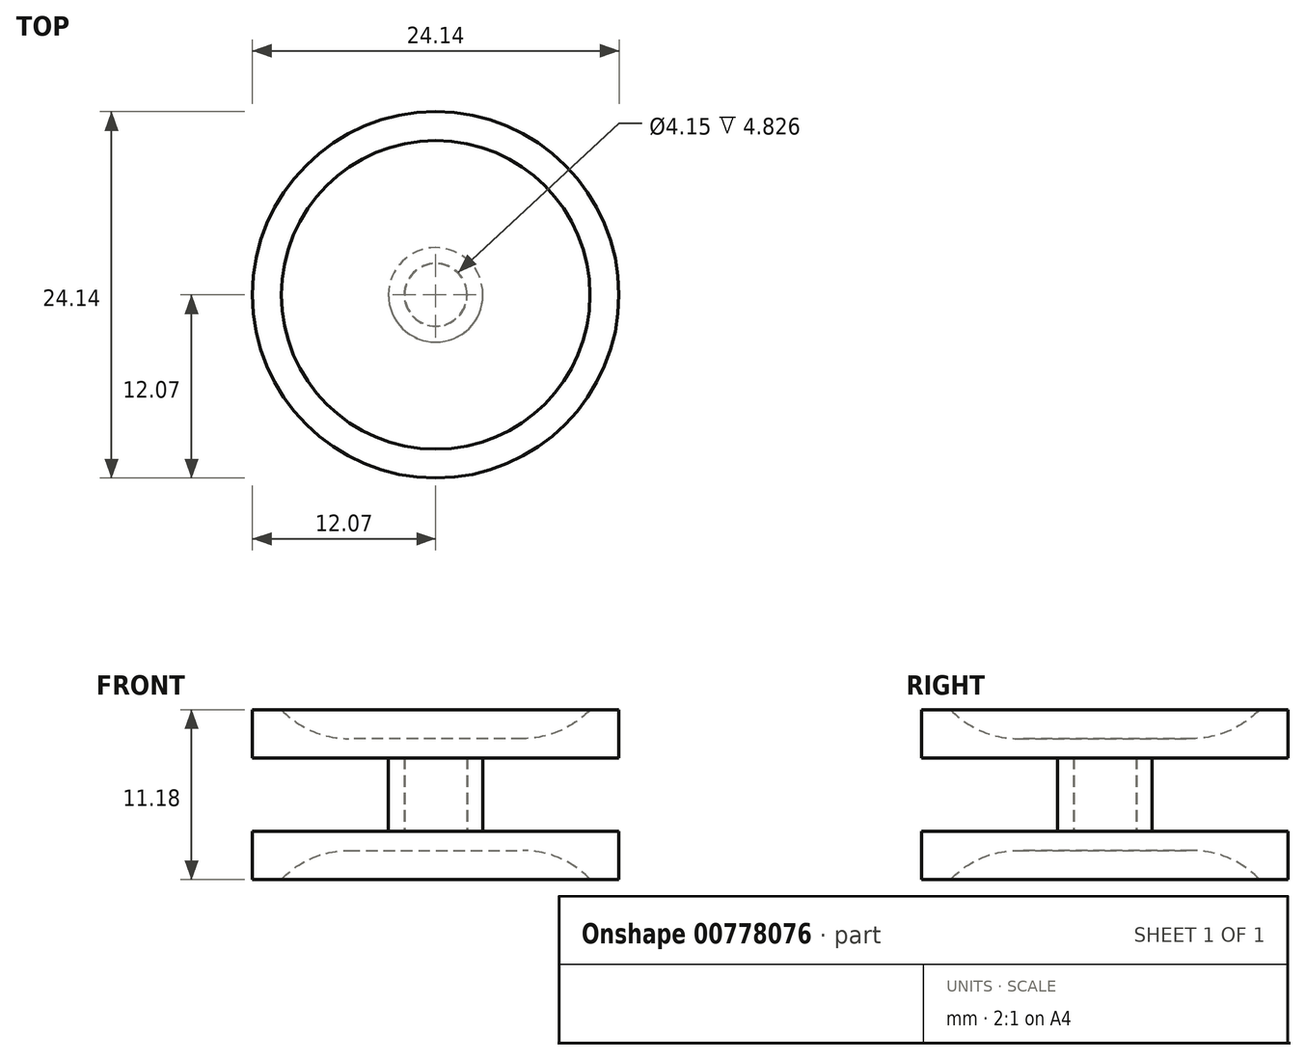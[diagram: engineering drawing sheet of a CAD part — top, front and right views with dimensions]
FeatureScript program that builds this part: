
annotation { "Feature Type Name" : "Feature", "Feature Type Description" : "" }
export const myFeature = defineFeature(function(context is Context, id is Id, definition is map)
    precondition{}
    {
        {
            var Q0;
            Q0=qCreatedBy(makeId("Top.planeOp"),FACE);
            var sketch = newSketch(context, id + "F0", { "sketchPlane" : qUnion([Q0])});
            skCircle(sketch, "E0", {"center": v(0, 0) * mm, "radius": 3.11 * mm});
            skCircle(sketch, "E1", {"center": v(0, 0) * mm, "radius": 2.07 * mm});
            skSolve(sketch);
        }
        {
            var Q0;
            Q0=qSketchRegion(id+"F0",true);
            extrude(context, id + "F1", {"entities" : qUnion([Q0]), "depth" : 4.83 * mm, "offsetDistance" : 25.4 * mm});
        }
        {
            var Q0;
            Q0=makeQuery(id+"F1.opExtrude","CAP_FACE",FACE,{"disambiguationData":[OSD([sQuery(id+"F0.wireOp",EDGE,"E0"),sQuery(id+"F0.wireOp",EDGE,"E1")])],"isStart":false});
            var sketch = newSketch(context, id + "F2", { "sketchPlane" : qUnion([Q0])});
            skCircle(sketch, "E2", {"center": v(0, 0) * mm, "radius": 12.07 * mm});
            skSolve(sketch);
        }
        {
            var Q0;
            Q0=qSketchRegion(id+"F2",true);
            extrude(context, id + "F3", {"entities" : qUnion([Q0]), "operationType" : NewBodyOperationType.ADD, "depth" : 3.17 * mm, "offsetDistance" : 25.4 * mm});
        }
        {
            var Q0;
            Q0=makeQuery(id+"F3.opExtrude","CAP_FACE",FACE,{"disambiguationData":[OSD([sQuery(id+"F2.wireOp",EDGE,"E2")])],"isStart":false});
            var sketch = newSketch(context, id + "F4", { "sketchPlane" : qUnion([Q0])});
            skCircle(sketch, "E3", {"center": v(0, 0) * mm, "radius": 10.16 * mm});
            skSolve(sketch);
        }
        {
            var Q0;
            Q0=qSketchRegion(id+"F4",true);
            extrude(context, id + "F5", {"entities" : qUnion([Q0]), "operationType" : NewBodyOperationType.REMOVE, "oppositeDirection" : true, "depth" : 1.9 * mm, "offsetDistance" : 25.4 * mm});
        }
        {
            var Q0;
            Q0=makeQuery(id+"F1.opExtrude","CAP_FACE",FACE,{"disambiguationData":[OSD([sQuery(id+"F0.wireOp",EDGE,"E0"),sQuery(id+"F0.wireOp",EDGE,"E1")])],"isStart":true});
            var sketch = newSketch(context, id + "F6", { "sketchPlane" : qUnion([Q0])});
            skCircle(sketch, "E4", {"center": v(0, 0) * mm, "radius": 2.05 * mm});
            skSolve(sketch);
        }
        {
            var Q0;
            Q0=qSketchRegion(id+"F6",true);
            extrude(context, id + "F7", {"entities" : qUnion([Q0]), "oppositeDirection" : true, "depth" : 4.83 * mm, "offsetDistance" : 25.4 * mm});
        }
        {
            var Q0;
            Q0=makeQuery(id+"F7.opExtrude","CAP_FACE",FACE,{"disambiguationData":[OSD([sQuery(id+"F6.wireOp",EDGE,"E4")])],"isStart":true});
            var sketch = newSketch(context, id + "F8", { "sketchPlane" : qUnion([Q0])});
            skCircle(sketch, "E5", {"center": v(0, 0) * mm, "radius": 12.07 * mm});
            skSolve(sketch);
        }
        {
            var Q0;
            Q0=qSketchRegion(id+"F8",true);
            extrude(context, id + "F9", {"entities" : qUnion([Q0]), "operationType" : NewBodyOperationType.ADD, "depth" : 3.17 * mm, "offsetDistance" : 25.4 * mm});
        }
        {
            var Q0;
            Q0=makeQuery(id+"F9.opExtrude","CAP_FACE",FACE,{"disambiguationData":[OSD([sQuery(id+"F8.wireOp",EDGE,"E5")])],"isStart":false});
            var sketch = newSketch(context, id + "F10", { "sketchPlane" : qUnion([Q0])});
            skCircle(sketch, "E6", {"center": v(0, 0) * mm, "radius": 10.16 * mm});
            skSolve(sketch);
        }
        {
            var Q0;
            Q0=qSketchRegion(id+"F10",true);
            extrude(context, id + "F11", {"entities" : qUnion([Q0]), "operationType" : NewBodyOperationType.REMOVE, "oppositeDirection" : true, "depth" : 1.9 * mm, "offsetDistance" : 25.4 * mm});
        }
        {
            var Q0;
            Q0=makeQuery(id+"F11.boolean.opBoolean","COPY",EDGE,{"derivedFrom":makeQuery(id+"F11.opExtrude","CAP_EDGE",EDGE,{"disambiguationData":[OSD([sQuery(id+"F10.wireOp",EDGE,"E6")])],"isStart":false})});
            var Q1;
            Q1=makeQuery(id+"F5.boolean.opBoolean","COPY",EDGE,{"derivedFrom":makeQuery(id+"F5.opExtrude","CAP_EDGE",EDGE,{"disambiguationData":[OSD([sQuery(id+"F4.wireOp",EDGE,"E3")])],"isStart":false})});
            fillet(context, id + "F12", {"entities" : qUnion([Q0, Q1]), "radius" : 6.1 * mm, "tangentPropagation" : true, "allowEdgeOverflow" : false});
        }
    });
